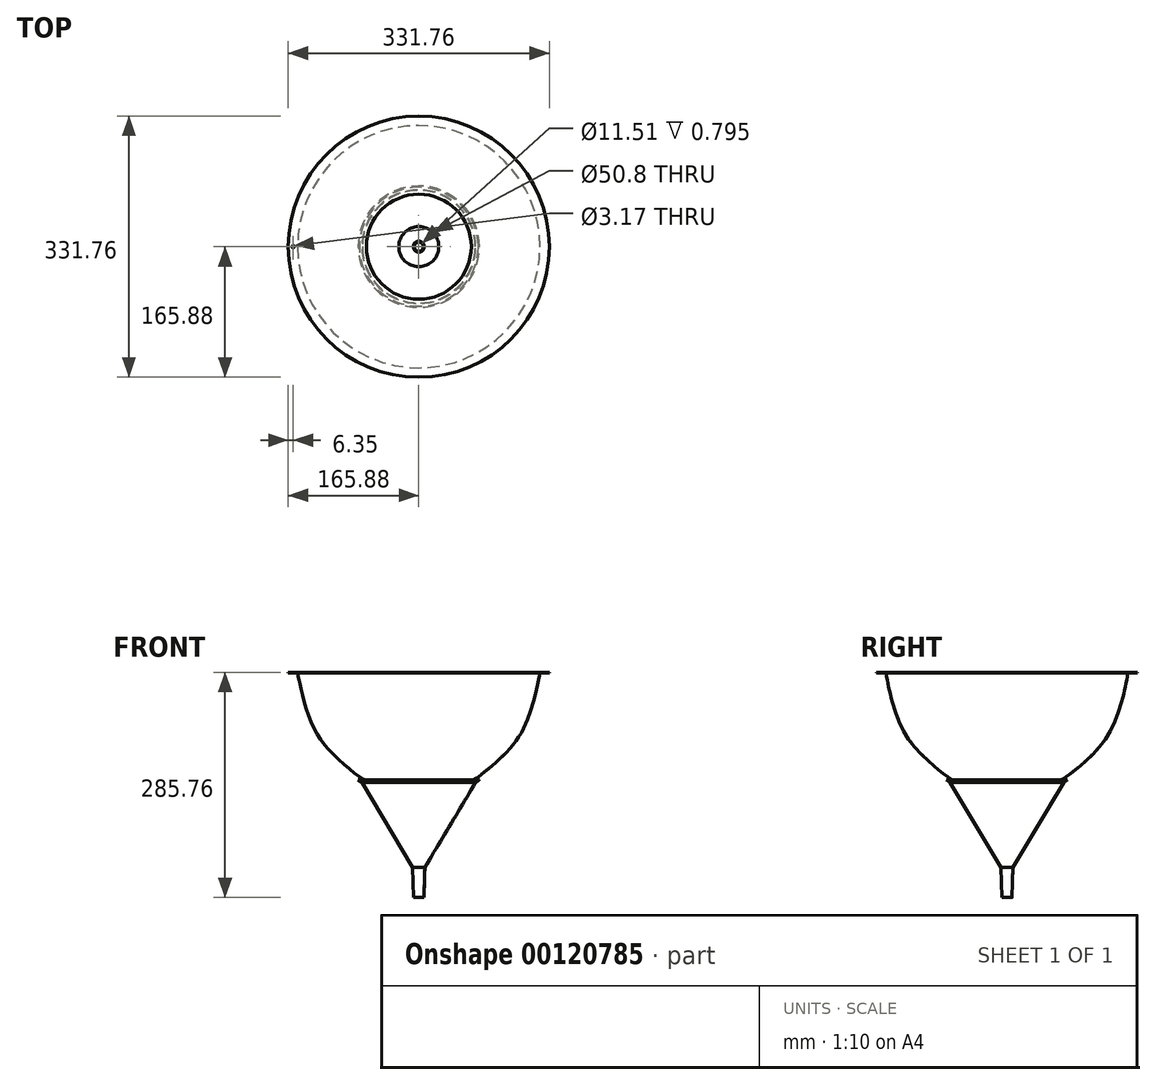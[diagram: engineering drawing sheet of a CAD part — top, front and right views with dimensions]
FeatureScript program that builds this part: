
annotation { "Feature Type Name" : "Feature", "Feature Type Description" : "" }
export const myFeature = defineFeature(function(context is Context, id is Id, definition is map)
    precondition{}
    {
        {
            var Q0;
            Q0=qCreatedBy(makeId("Front.planeOp"),FACE);
            var sketch = newSketch(context, id + "F0", { "sketchPlane" : qUnion([Q0])});
            skPoint(sketch, "E0", {"position": v(25.4, 0) * mm});
            skLineSegment(sketch, "E1", {"start": v(25.4, 0) * mm, "end": v(66.68, 0) * mm});
            skLineSegment(sketch, "E2.bottom", {"start": v(0, 0) * mm, "end": v(153.99, 0) * mm});
            skLineSegment(sketch, "E2.top", {"start": v(0, 136.53) * mm, "end": v(153.99, 136.53) * mm});
            skLineSegment(sketch, "E2.left", {"start": v(0, 0) * mm, "end": v(0, 136.53) * mm});
            skLineSegment(sketch, "E2.right", {"start": v(153.99, 0) * mm, "end": v(153.99, 136.53) * mm});
            skFitSpline(sketch, "E3", {"points": [v(66.68, 0) * mm, v(71.08, 1.14) * mm, v(105.1, 28.95) * mm, v(135.2, 69.7) * mm, v(150.82, 120.37) * mm, v(153.99, 136.53) * mm], "startDerivative": vector(44.47, 2.04) * mm, "endDerivative": vector(16.16, 90.75) * mm});
            skSolve(sketch);
        }
        {
            var Q0;
            Q0=makeQuery(id+"F0.imprint","IMPRINT",FACE,{"disambiguationData":[TD([[makeQuery(id+"F0.imprint","IMPRINT",EDGE,{"derivedFrom":sQuery(id+"F0.wireOp",EDGE,"E2.top")}),-1.0]])]});
            var Q1;
            Q1=sQuery(id+"F0.wireOp",EDGE,"E2.left");
            revolve(context, id + "F1", {"entities" : qUnion([Q0]), "axis" : qUnion([Q1]), "revolveType" : RevolveType.FULL});
        }
        {
            var Q0;
            Q0=makeQuery(id+"F1.opRevolve","SWEPT_FACE",FACE,{"disambiguationData":[OSD([sQuery(id+"F0.wireOp",EDGE,"E2.top")])]});
            shell(context, id + "F2", {"entities" : qUnion([Q0]), "thickness" : 0.8 * mm});
        }
        {
            var Q0;
            Q0=makeQuery(id+"F1.opRevolve","SWEPT_FACE",FACE,{"disambiguationData":[OSD([sQuery(id+"F0.wireOp",EDGE,"E2.top")])]});
            var sketch = newSketch(context, id + "F3", { "sketchPlane" : qUnion([Q0])});
            skCircle(sketch, "E4", {"center": v(0, 0) * mm, "radius": 165.88 * mm});
            skSolve(sketch);
        }
        {
            var Q0;
            Q0=makeQuery(id+"F3.imprint","IMPRINT",FACE,{"disambiguationData":[TD([[makeQuery(id+"F3.imprint","IMPRINT",EDGE,{"derivedFrom":sQuery(id+"F3.wireOp",EDGE,"E4")}),1.0]])]});
            var Q1;
            {var subQ0=sQuery(id+"F0.wireOp",EDGE,"E3");var subQ1=sQuery(id+"F0.wireOp",EDGE,"E2.right");var subQ2=sQuery(id+"F0.wireOp",EDGE,"E2.top");Q1=makeQuery(id+"F3.imprint","IMPRINT",FACE,{"disambiguationData":[TD([[makeQuery(id+"F3.imprint","IMPRINT",EDGE,{"derivedFrom":makeQuery(id+"F1.opRevolve","SWEPT_EDGE",EDGE,{"disambiguationData":[OSD([subQ2,subQ1,subQ0])]})}),-1.0]])]});}
            extrude(context, id + "F4", {"entities" : qUnion([Q0, Q1]), "operationType" : NewBodyOperationType.ADD, "oppositeDirection" : true, "depth" : 0.8 * mm});
        }
        {
            var Q0;
            Q0=makeQuery(id+"F2.opShell","OFFSET_EDGE",EDGE,{"disambiguationData":[OSD([sQuery(id+"F0.wireOp",EDGE,"E2.top"),sQuery(id+"F0.wireOp",EDGE,"E2.right"),sQuery(id+"F0.wireOp",EDGE,"E3")])]});
            fillet(context, id + "F5", {"entities" : qUnion([Q0]), "radius" : 0.5 * mm, "tangentPropagation" : true, "allowEdgeOverflow" : false});
        }
        {
            var Q0;
            Q0=makeQuery(id+"F2.opShell","OFFSET_FACE",FACE,{"disambiguationData":[OSD([sQuery(id+"F0.wireOp",EDGE,"E2.bottom")])]});
            var sketch = newSketch(context, id + "F6", { "sketchPlane" : qUnion([Q0])});
            skCircle(sketch, "E5", {"center": v(0, 0) * mm, "radius": 25.4 * mm});
            skSolve(sketch);
        }
        {
            var Q0;
            Q0=makeQuery(id+"F6.imprint","IMPRINT",FACE,{"disambiguationData":[TD([[makeQuery(id+"F6.imprint","IMPRINT",EDGE,{"derivedFrom":sQuery(id+"F6.wireOp",EDGE,"E5")}),1.0]])]});
            extrude(context, id + "F7", {"entities" : qUnion([Q0]), "operationType" : NewBodyOperationType.REMOVE, "oppositeDirection" : true, "depth" : 0.8 * mm});
        }
        {
            var Q0;
            Q0=qCreatedBy(makeId("Front.planeOp"),FACE);
            var sketch = newSketch(context, id + "F8", { "sketchPlane" : qUnion([Q0])});
            skPoint(sketch, "E6", {"position": v(72.23, -3.18) * mm});
            skLineSegment(sketch, "E7.bottom", {"start": v(0, 0) * mm, "end": v(72.23, 0) * mm});
            skLineSegment(sketch, "E7.top", {"start": v(0, -149.23) * mm, "end": v(72.23, -149.23) * mm});
            skLineSegment(sketch, "E7.left", {"start": v(0, 0) * mm, "end": v(0, -149.23) * mm});
            skLineSegment(sketch, "E7.right", {"start": v(72.23, 0) * mm, "end": v(72.23, -149.23) * mm});
            skPoint(sketch, "E8", {"position": v(77, 0) * mm});
            skPoint(sketch, "E9", {"position": v(6.55, -149.23) * mm});
            skPoint(sketch, "E10", {"position": v(7.74, -111.13) * mm});
            skLineSegment(sketch, "E11", {"start": v(6.55, -149.23) * mm, "end": v(7.74, -111.13) * mm});
            skLineSegment(sketch, "E12", {"start": v(7.74, -111.13) * mm, "end": v(72.23, -3.17) * mm});
            skLineSegment(sketch, "E13", {"start": v(77, 0) * mm, "end": v(72.23, -3.18) * mm});
            skLineSegment(sketch, "E14", {"start": v(77, 0) * mm, "end": v(72.23, 0) * mm});
            skSolve(sketch);
        }
        {
            var Q0;
            {var subQ2=sQuery(id+"F8.wireOp",EDGE,"E13");Q0=makeQuery(id+"F8.imprint","IMPRINT",FACE,{"disambiguationData":[TD([[makeQuery(id+"F8.imprint","IMPRINT",EDGE,{"derivedFrom":subQ2}),-1.0]])]});}
            var Q1;
            {var subQ1=sQuery(id+"F8.wireOp",EDGE,"E7.bottom");Q1=makeQuery(id+"F8.imprint","IMPRINT",FACE,{"disambiguationData":[TD([[makeQuery(id+"F8.imprint","IMPRINT",EDGE,{"derivedFrom":subQ1}),-1.0]])]});}
            var Q2;
            Q2=sQuery(id+"F8.wireOp",EDGE,"E7.left");
            revolve(context, id + "F9", {"entities" : qUnion([Q0, Q1]), "axis" : qUnion([Q2]), "revolveType" : RevolveType.FULL});
        }
        {
            var Q0;
            Q0=makeQuery(id+"F9.opRevolve","SWEPT_FACE",FACE,{"disambiguationData":[OSD([sQuery(id+"F8.wireOp",EDGE,"E7.bottom"),sQuery(id+"F8.wireOp",EDGE,"E14")])]});
            shell(context, id + "F10", {"entities" : qUnion([Q0]), "thickness" : 0.8 * mm});
        }
        {
            var Q0;
            Q0=makeQuery(id+"F10.opShell","OFFSET_FACE",FACE,{"disambiguationData":[OSD([sQuery(id+"F8.wireOp",EDGE,"E7.top")])]});
            var sketch = newSketch(context, id + "F11", { "sketchPlane" : qUnion([Q0])});
            skCircle(sketch, "E15", {"center": v(0, 0) * mm, "radius": 5.75 * mm});
            skSolve(sketch);
        }
        {
            var Q0;
            Q0=makeQuery(id+"F11.imprint","IMPRINT",FACE,{"disambiguationData":[TD([[makeQuery(id+"F11.imprint","IMPRINT",EDGE,{"derivedFrom":sQuery(id+"F11.wireOp",EDGE,"E15")}),1.0]])]});
            extrude(context, id + "F12", {"entities" : qUnion([Q0]), "operationType" : NewBodyOperationType.REMOVE, "oppositeDirection" : true, "depth" : 0.8 * mm});
        }
        {
            var Q0;
            {var subQ0=sQuery(id+"F0.wireOp",EDGE,"E2.top");Q0=makeQuery(id+"F4.boolean.opBoolean","MERGE",FACE,{"derivedFrom":[makeQuery(id+"F1.opRevolve","SWEPT_FACE",FACE,{"disambiguationData":[OSD([subQ0])]}),makeQuery(id+"F4.opExtrude","CAP_FACE",FACE,{"disambiguationData":[OSD([subQ0,sQuery(id+"F0.wireOp",EDGE,"E2.right"),sQuery(id+"F0.wireOp",EDGE,"E3"),sQuery(id+"F3.wireOp",EDGE,"E4")])],"isStart":true})]});}
            var sketch = newSketch(context, id + "F13", { "sketchPlane" : qUnion([Q0])});
            skPoint(sketch, "E16", {"position": v(-159.53, 0) * mm});
            skSolve(sketch);
        }
        {
            var Q0;
            Q0=sQuery(id+"F13.wireOp",VERTEX,"E16");
            var Q1;
            Q1=makeQuery(id+"F1.opRevolve","SWEPT_BODY",BODY,{"disambiguationData":[OSD([sQuery(id+"F0.wireOp",EDGE,"E2.bottom"),sQuery(id+"F0.wireOp",EDGE,"E2.top"),sQuery(id+"F0.wireOp",EDGE,"E2.left"),sQuery(id+"F0.wireOp",EDGE,"E3")])]});
            hole(context, id + "F14", {"style" : HoleStyle.SIMPLE, "endStyle" : HoleEndStyle.BLIND, "holeDiameter" : 3.17 * mm, "holeDepth" : 25.4 * mm, "locations" : qUnion([Q0]), "scope" : qUnion([Q1])});
        }
    });
